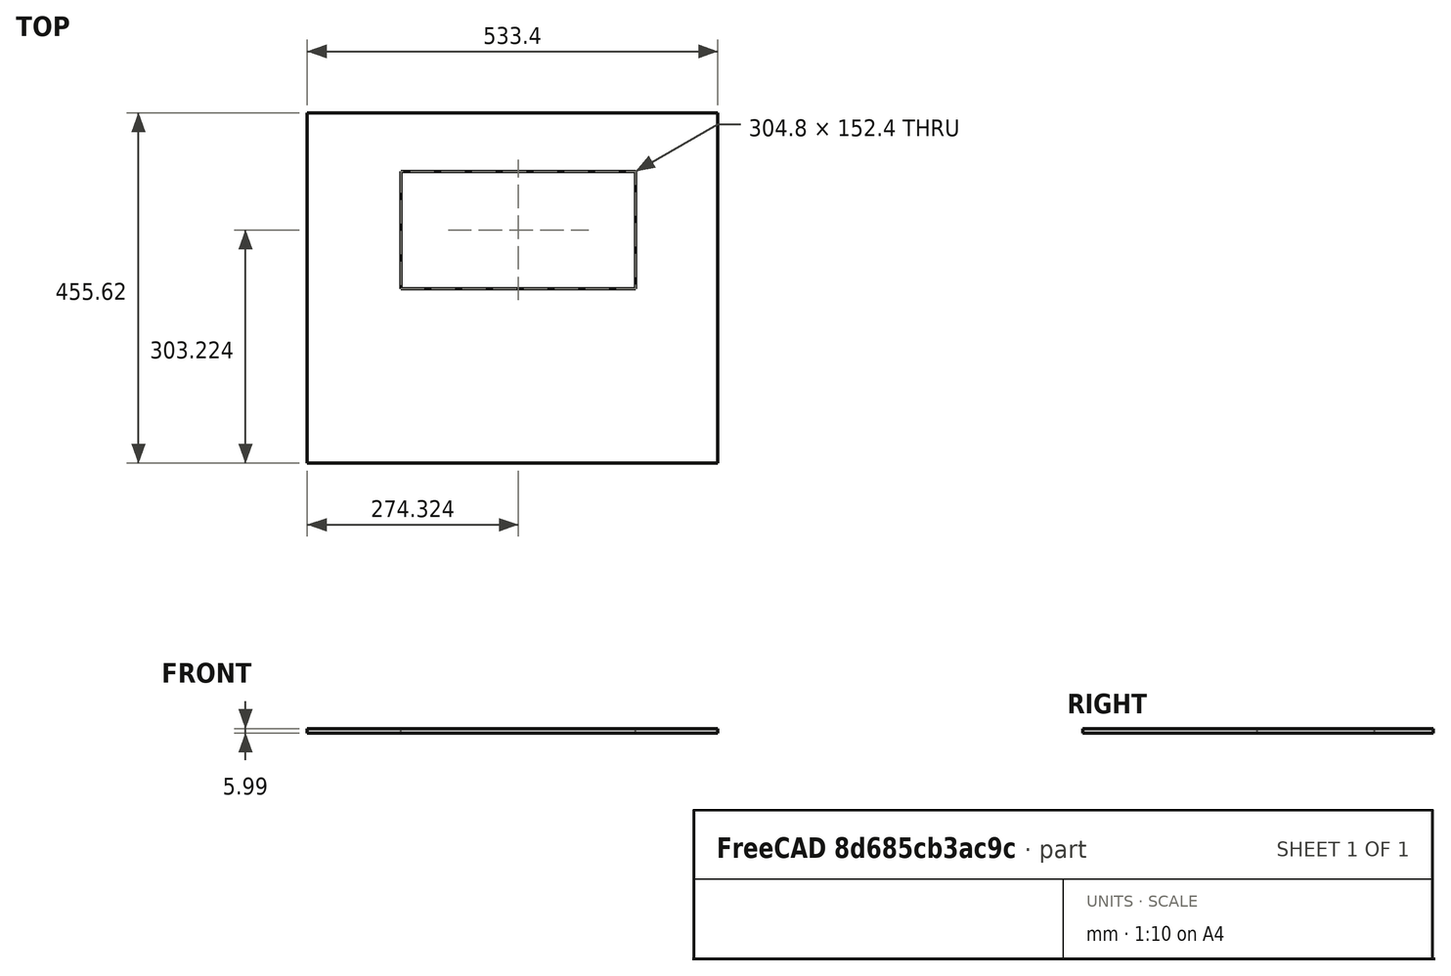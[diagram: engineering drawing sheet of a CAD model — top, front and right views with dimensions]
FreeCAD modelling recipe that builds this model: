
FCSTD DOCUMENT  (FreeCAD 0.19R24267 (Git))
Label: Up1-P11
License: All rights reserved
LicenseURL: http://en.wikipedia.org/wiki/All_rights_reserved
objects: TechDraw::DrawViewDimension×7, TechDraw::DrawProjGroupItem×2, TechDraw::DrawHatch×2, TechDraw::DrawViewAnnotation×2, Sketcher::SketchObject×1, Part::Extrusion×1, TechDraw::DrawSVGTemplate×1, TechDraw::DrawProjGroup×1, TechDraw::DrawPage×1
note: 2 computed .brp shape members not serialized (recipe doc carries the construction recipe); baked Part::Feature solids carry a one-line shape summary decoded from their .brp

FEATURE [Sketcher::SketchObject] Sketch
  FullyConstrained = false
  sketch-geometry (8):
    g0: LineSegment StartX=-284.196 StartY=107.544 StartZ=0 EndX=249.204 EndY=107.544 EndZ=0
    g1: LineSegment StartX=249.204 StartY=107.544 StartZ=0 EndX=249.204 EndY=-348.082 EndZ=0
    g2: LineSegment StartX=249.204 StartY=-348.082 StartZ=0 EndX=-284.196 EndY=-348.082 EndZ=0
    g3: LineSegment StartX=-284.196 StartY=-348.082 StartZ=0 EndX=-284.196 EndY=107.544 EndZ=0
    g4: LineSegment StartX=-162.276 StartY=31.3436 StartZ=0 EndX=142.524 EndY=31.3436 EndZ=0
    g5: LineSegment StartX=142.524 StartY=31.3436 StartZ=0 EndX=142.524 EndY=-121.056 EndZ=0
    g6: LineSegment StartX=142.524 StartY=-121.056 StartZ=0 EndX=-162.276 EndY=-121.056 EndZ=0
    g7: LineSegment StartX=-162.276 StartY=-121.056 StartZ=0 EndX=-162.276 EndY=31.3436 EndZ=0
  constraints (22):
    c: Coincident(g0,g1)
    c: Coincident(g1,g2)
    c: Coincident(g2,g3)
    c: Coincident(g3,g0)
    c: Horizontal(g0)
    c: Horizontal(g2)
    c: Vertical(g1)
    c: Vertical(g3)
    c: DistanceY(g3,g3) = 455.625
    c: DistanceX(g0,g0) = 533.4
    c: Coincident(g4,g5)
    c: Coincident(g5,g6)
    c: Coincident(g6,g7)
    c: Coincident(g7,g4)
    c: Horizontal(g4)
    c: Horizontal(g6)
    c: Vertical(g5)
    c: Vertical(g7)
    c: DistanceY(g7,g7) = 152.4
    c: DistanceX(g4,g4) = 304.8
    c: Distance(g4,g0) = 76.2
    c: Distance(g6,g3) = 121.92
FEATURE [Part::Extrusion] Extrude
  Base = -> Sketch
  Dir = (0,0,1)
  DirMode = 2
  FaceMakerClass = Part::FaceMakerBullseye
  LengthFwd = 5.9944
  LengthRev = 0
  Solid = true
  Symmetric = false
FEATURE [TechDraw::DrawSVGTemplate] Template
  Height = 215.9
  Orientation = 1
  Width = 279.4
FEATURE [TechDraw::DrawProjGroupItem] ProjItem  label="Front"
  CoarseView = false
  Direction = (0,0,1)
  Focus = 100
  HardHidden = false
  IsoCount = 0
  IsoHidden = false
  IsoVisible = false
  LockPosition = true
  Perspective = false
  Rotation = 0
  RotationVector = (1,0,0)
  Scale = 0.25
  ScaleType = 2
  SeamHidden = false
  SeamVisible = true
  SmoothHidden = false
  SmoothVisible = true
  Source = -> [Extrude]
  Type = 0
  X = 0
  XDirection = (1,0,0)
  Y = 0
FEATURE [TechDraw::DrawProjGroupItem] ProjItem001  label="Left"
  CoarseView = false
  Direction = (-1,0,1e-16)
  Focus = 100
  HardHidden = false
  IsoCount = 0
  IsoHidden = false
  IsoVisible = false
  LockPosition = false
  Perspective = false
  Rotation = 0
  RotationVector = (1,0,0)
  Scale = 0.25
  ScaleType = 2
  SeamHidden = false
  SeamVisible = true
  SmoothHidden = false
  SmoothVisible = true
  Source = -> [Extrude]
  Type = 1
  X = 100.69
  XDirection = (1e-16,0,1)
  Y = 0
FEATURE [TechDraw::DrawProjGroup] ProjGroup
  Anchor = -> ProjItem
  AutoDistribute = true
  LockPosition = false
  ProjectionType = 0
  Rotation = 0
  Scale = 0.25
  ScaleType = 2
  Source = -> [Extrude]
  Views = -> [ProjItem,ProjItem001]
  X = 131.076
  Y = 104.722
  spacingX = 15.0114
  spacingY = 15.0114
FEATURE [TechDraw::DrawHatch] Hatch  label="HatchF0"
  HatchPattern = <path>
  Source = -> ProjItem [Face0]
FEATURE [TechDraw::DrawHatch] Hatch001  label="Hatch001F0"
  HatchPattern = <path>
  Source = -> ProjItem001 [Face0]
FEATURE [TechDraw::DrawViewDimension] Dimension
  Arbitrary = false
  ArbitraryTolerances = false
  EqualTolerance = true
  FormatSpec = %.3f
  FormatSpecOverTolerance = %+.3f
  FormatSpecUnderTolerance = %+.3f
  Inverted = false
  LockPosition = false
  MeasureType = 1
  OverTolerance = 0
  References2D = -> [ProjItem]
  Rotation = 0
  ScaleType = 0
  TheoreticalExact = false
  Type = 1
  UnderTolerance = 0
  X = 1.67878
  Y = 71.8768
FEATURE [TechDraw::DrawViewDimension] Dimension001
  Arbitrary = false
  ArbitraryTolerances = false
  EqualTolerance = true
  FormatSpec = %.3f
  FormatSpecOverTolerance = %+.3f
  FormatSpecUnderTolerance = %+.3f
  Inverted = false
  LockPosition = false
  MeasureType = 1
  OverTolerance = 0
  References2D = -> [ProjItem]
  Rotation = 0
  ScaleType = 0
  TheoreticalExact = false
  Type = 2
  UnderTolerance = 0
  X = 78.1467
  Y = 0.279797
FEATURE [TechDraw::DrawViewDimension] Dimension002
  Arbitrary = false
  ArbitraryTolerances = false
  EqualTolerance = true
  FormatSpec = %.3f
  FormatSpecOverTolerance = %+.3f
  FormatSpecUnderTolerance = %+.3f
  Inverted = false
  LockPosition = false
  MeasureType = 1
  OverTolerance = 0
  References2D = -> [ProjItem001]
  Rotation = 0
  ScaleType = 0
  TheoreticalExact = false
  Type = 1
  UnderTolerance = 0
  X = 16.5261
  Y = 36.0132
FEATURE [TechDraw::DrawViewDimension] Dimension003
  Arbitrary = false
  ArbitraryTolerances = false
  EqualTolerance = true
  FormatSpec = %.3f
  FormatSpecOverTolerance = %+.3f
  FormatSpecUnderTolerance = %+.3f
  Inverted = false
  LockPosition = false
  MeasureType = 1
  OverTolerance = 0
  References2D = -> [ProjItem]
  Rotation = 0
  ScaleType = 0
  TheoreticalExact = false
  Type = 1
  UnderTolerance = 0
  X = 1.84987
  Y = 49.0645
FEATURE [TechDraw::DrawViewDimension] Dimension004
  Arbitrary = false
  ArbitraryTolerances = false
  EqualTolerance = true
  FormatSpec = %.3f
  FormatSpecOverTolerance = %+.3f
  FormatSpecUnderTolerance = %+.3f
  Inverted = false
  LockPosition = false
  MeasureType = 1
  OverTolerance = 0
  References2D = -> [ProjItem]
  Rotation = 0
  ScaleType = 0
  TheoreticalExact = false
  Type = 2
  UnderTolerance = 0
  X = 49.486
  Y = 21.9425
FEATURE [TechDraw::DrawViewDimension] Dimension005
  Arbitrary = false
  ArbitraryTolerances = false
  EqualTolerance = true
  FormatSpec = %.3f
  FormatSpecOverTolerance = %+.3f
  FormatSpecUnderTolerance = %+.3f
  Inverted = false
  LockPosition = false
  MeasureType = 1
  OverTolerance = 0
  References2D = -> [ProjItem]
  Rotation = 0
  ScaleType = 0
  TheoreticalExact = false
  Type = 2
  UnderTolerance = 0
  X = 49.7516
  Y = 49.8164
FEATURE [TechDraw::DrawViewDimension] Dimension006
  Arbitrary = false
  ArbitraryTolerances = false
  EqualTolerance = true
  FormatSpec = %.3f
  FormatSpecOverTolerance = %+.3f
  FormatSpecUnderTolerance = %+.3f
  Inverted = false
  LockPosition = false
  MeasureType = 1
  OverTolerance = 0
  References2D = -> [ProjItem]
  Rotation = 0
  ScaleType = 0
  TheoreticalExact = false
  Type = 1
  UnderTolerance = 0
  X = -51.7148
  Y = 26.7113
FEATURE [TechDraw::DrawViewAnnotation] Annotation
  Font = osifont
  LineSpace = 80
  LockPosition = false
  MaxWidth = -1
  Rotation = 0
  ScaleType = 0
  Text = Figure S3 (Upright) | Panel 11 [front right] | Quantity: 1
  TextSize = 5.0038
  TextStyle = 0
  X = 31.4001
  Y = 195.58
FEATURE [TechDraw::DrawViewAnnotation] Annotation002
  Font = osifont
  LineSpace = 80
  LockPosition = false
  MaxWidth = -1
  Rotation = 0
  ScaleType = 0
  Text = Units: Inches
  TextSize = 5.0038
  TextStyle = 0
  X = 259.08
  Y = 5.08
FEATURE [TechDraw::DrawPage] Page
  KeepUpdated = true
  NextBalloonIndex = 1
  ProjectionType = 0
  Template = -> Template
  Views = -> [ProjGroup,Dimension,Dimension001,Dimension002,Dimension003,Dimension004,Dimension005,Dimension006,Annotation,Annotation002]
note: 2 file-system paths scrubbed to <path> (originals preserved in the JSON sidecar)
